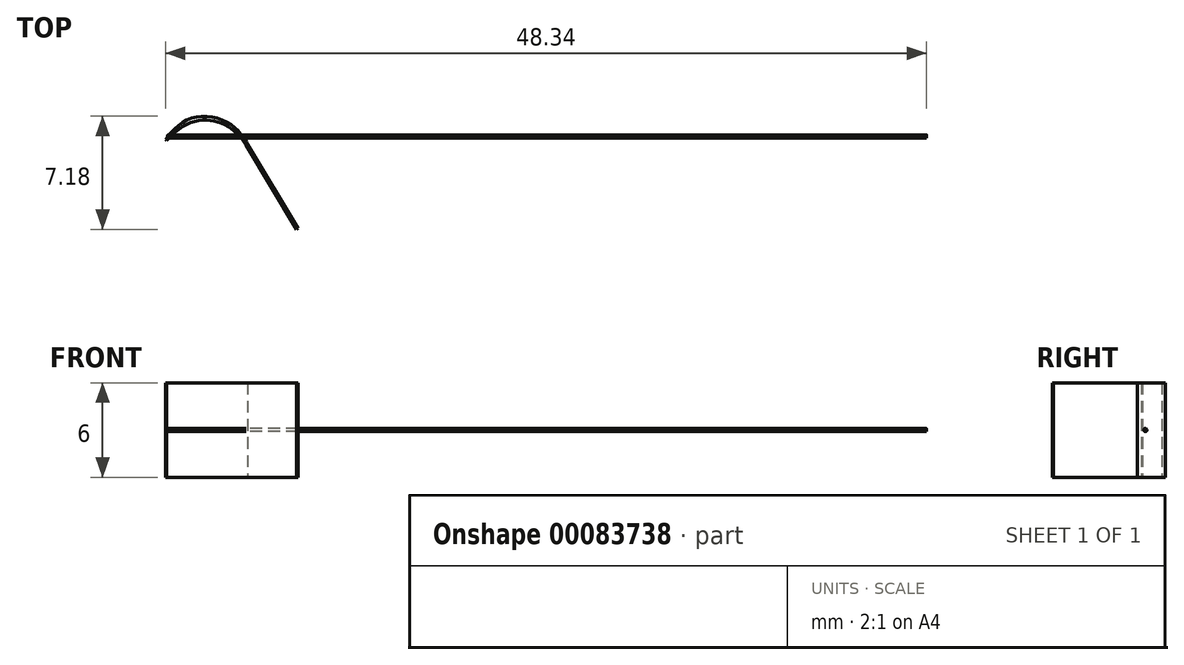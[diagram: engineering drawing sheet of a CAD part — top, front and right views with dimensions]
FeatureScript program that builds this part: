
annotation { "Feature Type Name" : "Feature", "Feature Type Description" : "" }
export const myFeature = defineFeature(function(context is Context, id is Id, definition is map)
    precondition{}
    {
        {
            var Q0;
            Q0=qCreatedBy(makeId("Top.planeOp"),FACE);
            var sketch = newSketch(context, id + "F0", { "sketchPlane" : qUnion([Q0])});
            skLineSegment(sketch, "E0", {"start": v(-8.26, 5.64) * mm, "end": v(0, 0) * mm, "construction": true});
            skFitSpline(sketch, "E1", {"points": [v(-8.26, 5.64) * mm, v(-3.2, 5.34) * mm], "startDerivative": vector(5.63, 6.66) * mm, "endDerivative": vector(2.8, -4.65) * mm});
            skLineSegment(sketch, "E2", {"start": v(-3.2, 5.34) * mm, "end": v(0, 0) * mm});
            skLineSegment(sketch, "E3.0", {"start": v(-3.12, 5.4) * mm, "end": v(0.09, 0.05) * mm});
            skFitSpline(sketch, "E3.1", {"points": [v(-8.34, 5.7) * mm, v(-7.86, 6.27) * mm, v(-6.85, 7) * mm, v(-5.33, 7.12) * mm, v(-4, 6.51) * mm, v(-3.36, 5.8) * mm, v(-3.12, 5.4) * mm]});
            skLineSegment(sketch, "E4", {"start": v(-8.34, 5.7) * mm, "end": v(-8.26, 5.64) * mm});
            skLineSegment(sketch, "E5", {"start": v(0, 0) * mm, "end": v(0.09, 0.05) * mm});
            skSolve(sketch);
        }
        {
            var Q0;
            Q0 = qSketchRegion(id + "F0", true);
            extrude(context, id + "F1", {"entities" : qUnion([Q0]), "endBound" : BoundingType.SYMMETRIC, "depth" : 6 * mm});
        }
        {
            var Q0;
            Q0=qCreatedBy(makeId("Right.planeOp"),FACE);
            cPlane(context, id + "F2", {"entities" : qUnion([Q0]), "cplaneType" : CPlaneType.OFFSET, "offset" : 0 * mm, "width" : 150 * mm, "height" : 150 * mm});
        }
        {
            var Q0;
            Q0=qCreatedBy(id+"F2.planeOp",FACE);
            var sketch = newSketch(context, id + "F3", { "sketchPlane" : qUnion([Q0])});
            skCircle(sketch, "E6", {"center": v(5.9, 0) * mm, "radius": 0.1 * mm});
            skLineSegment(sketch, "E7", {"start": v(5.4, 0) * mm, "end": v(0, 0) * mm, "construction": true});
            skSolve(sketch);
        }
        {
            var Q0;
            Q0=makeQuery(id+"F3.imprint","IMPRINT",FACE,{"disambiguationData":[TD([[makeQuery(id+"F3.imprint","IMPRINT",EDGE,{"derivedFrom":sQuery(id+"F3.wireOp",EDGE,"E6")}),1.0]])]});
            extrude(context, id + "F4", {"entities" : qUnion([Q0]), "depth" : 40 * mm, "hasSecondDirection" : true, "secondDirectionOppositeDirection" : true, "secondDirectionDepth" : 8.2 * mm});
        }
    });
